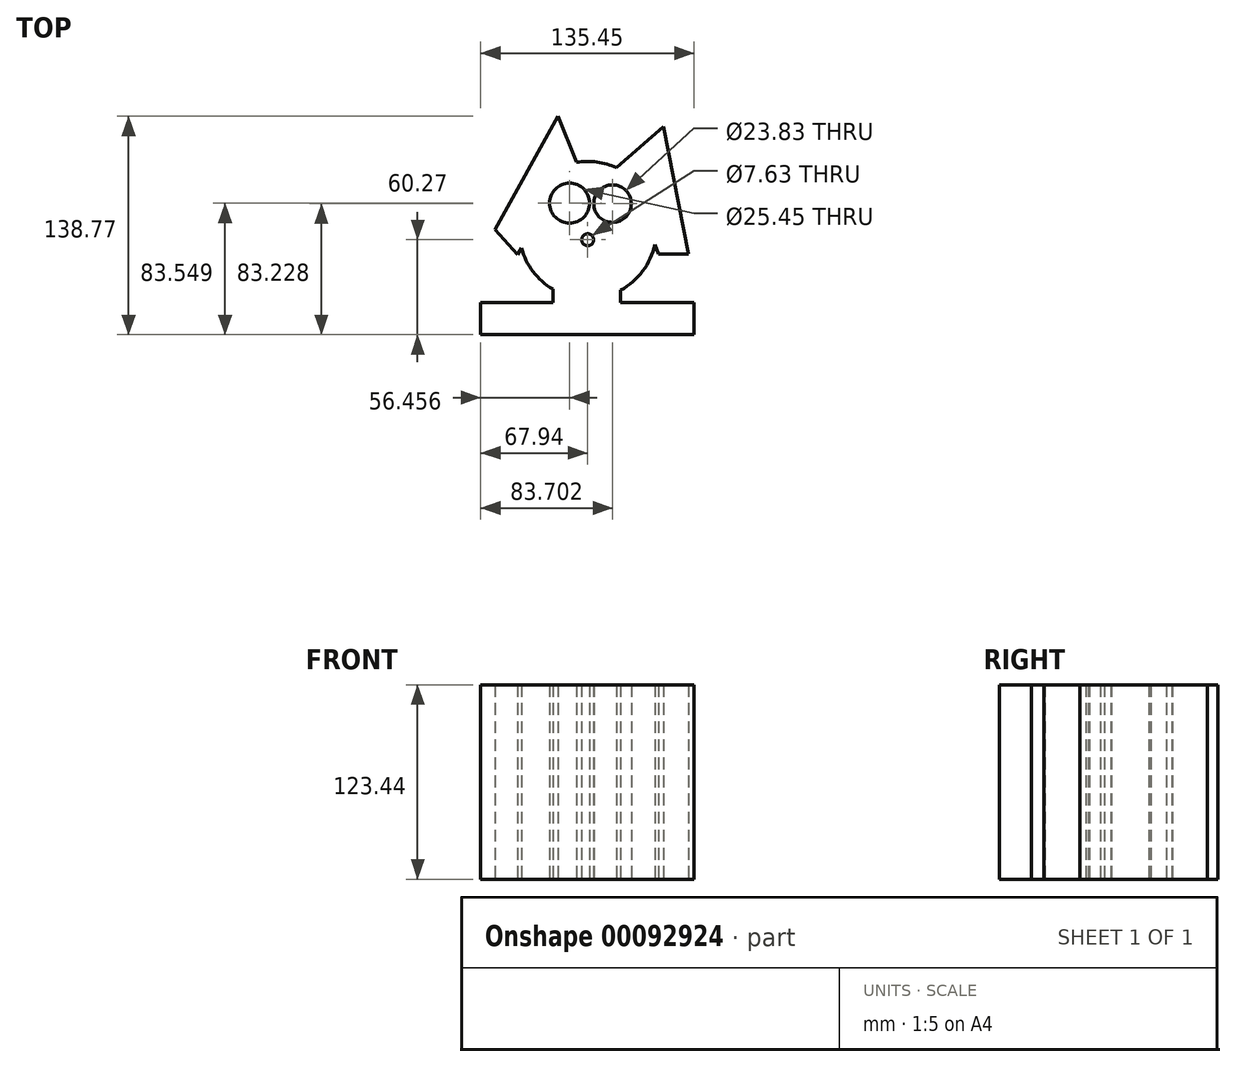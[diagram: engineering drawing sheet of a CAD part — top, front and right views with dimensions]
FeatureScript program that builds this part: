
annotation { "Feature Type Name" : "Feature", "Feature Type Description" : "" }
export const myFeature = defineFeature(function(context is Context, id is Id, definition is map)
    precondition{}
    {
        {
            var Q0;
            Q0=qCreatedBy(makeId("Top.planeOp"),FACE);
            var sketch = newSketch(context, id + "F0", { "sketchPlane" : qUnion([Q0])});
            skLineSegment(sketch, "E0", {"start": v(-54.1, -53.02) * mm, "end": v(67.49, -53.02) * mm});
            skLineSegment(sketch, "E1", {"start": v(-54.1, -53.02) * mm, "end": v(-67.94, -53.02) * mm});
            skLineSegment(sketch, "E2", {"start": v(-67.94, -53.02) * mm, "end": v(-67.94, -73.29) * mm});
            skLineSegment(sketch, "E3", {"start": v(-67.94, -73.29) * mm, "end": v(67.51, -73.29) * mm});
            skLineSegment(sketch, "E4", {"start": v(67.51, -73.29) * mm, "end": v(67.49, -53.02) * mm});
            skCircle(sketch, "E5", {"center": v(0, -6.83) * mm, "radius": 43.59 * mm});
            skLineSegment(sketch, "E6", {"start": v(-7.03, 36.18) * mm, "end": v(-18.79, 65.48) * mm});
            skLineSegment(sketch, "E7", {"start": v(-18.79, 65.48) * mm, "end": v(-58.85, -6.5) * mm});
            skLineSegment(sketch, "E8", {"start": v(-58.85, -6.5) * mm, "end": v(-44.51, -22.5) * mm});
            skLineSegment(sketch, "E9", {"start": v(-44.51, -22.5) * mm, "end": v(-42.05, -18.3) * mm});
            skLineSegment(sketch, "E10", {"start": v(18.24, 32.75) * mm, "end": v(48.08, 59) * mm});
            skLineSegment(sketch, "E11", {"start": v(48.08, 59) * mm, "end": v(63.95, -22.14) * mm});
            skLineSegment(sketch, "E12", {"start": v(63.95, -22.14) * mm, "end": v(45.06, -22.14) * mm});
            skLineSegment(sketch, "E13", {"start": v(45.06, -22.14) * mm, "end": v(42.61, -16) * mm});
            skLineSegment(sketch, "E14.trimOffspring", {"start": v(-10.56, 35.46) * mm, "end": v(-8.29, 39.32) * mm});
            skLineSegment(sketch, "E15.trimOffspring", {"start": v(24.59, 29.16) * mm, "end": v(21.88, 35.95) * mm});
            skLineSegment(sketch, "E16", {"start": v(-22.19, -44.35) * mm, "end": v(-22.19, -53.02) * mm});
            skLineSegment(sketch, "E17", {"start": v(20.97, -45.05) * mm, "end": v(20.97, -53.02) * mm});
            skCircle(sketch, "E18", {"center": v(-11.48, 10.26) * mm, "radius": 12.72 * mm});
            skCircle(sketch, "E19", {"center": v(15.76, 9.94) * mm, "radius": 11.91 * mm});
            skCircle(sketch, "E20", {"center": v(0, -13.02) * mm, "radius": 3.82 * mm});
            skLineSegment(sketch, "E21", {"start": v(-16.56, -13.02) * mm, "end": v(-32.99, -6.5) * mm});
            skLineSegment(sketch, "E22", {"start": v(-16.56, -16.95) * mm, "end": v(-34.9, -15.03) * mm});
            skLineSegment(sketch, "E23", {"start": v(-17.63, -16) * mm, "end": v(-34.7, -11.4) * mm});
            skPoint(sketch, "E23.startSnap0", {"position": v(-25.73, -16) * mm});
            skLineSegment(sketch, "E24", {"start": v(-20.19, -13.7) * mm, "end": v(-35.56, -7.6) * mm});
            skPoint(sketch, "E24.startSnap0", {"position": v(-26.16, -13.7) * mm});
            skLineSegment(sketch, "E25", {"start": v(17.2, -16.3) * mm, "end": v(30.87, -10.56) * mm});
            skLineSegment(sketch, "E26", {"start": v(17.2, -18.06) * mm, "end": v(32.42, -14.09) * mm});
            skLineSegment(sketch, "E27", {"start": v(18.69, -17.67) * mm, "end": v(32.86, -17.67) * mm});
            skLineSegment(sketch, "E28", {"start": v(15.24, -13.43) * mm, "end": v(28.92, -7.69) * mm});
            skPoint(sketch, "E28.startSnap0", {"position": v(24.03, -13.43) * mm});
            skSolve(sketch);
        }
        {
            var Q0;
            Q0 = qSketchRegion(id + "F0", true);
            extrude(context, id + "F1", {"entities" : qUnion([Q0]), "endBound" : BoundingType.SYMMETRIC, "depth" : 123.44 * mm});
        }
    });
